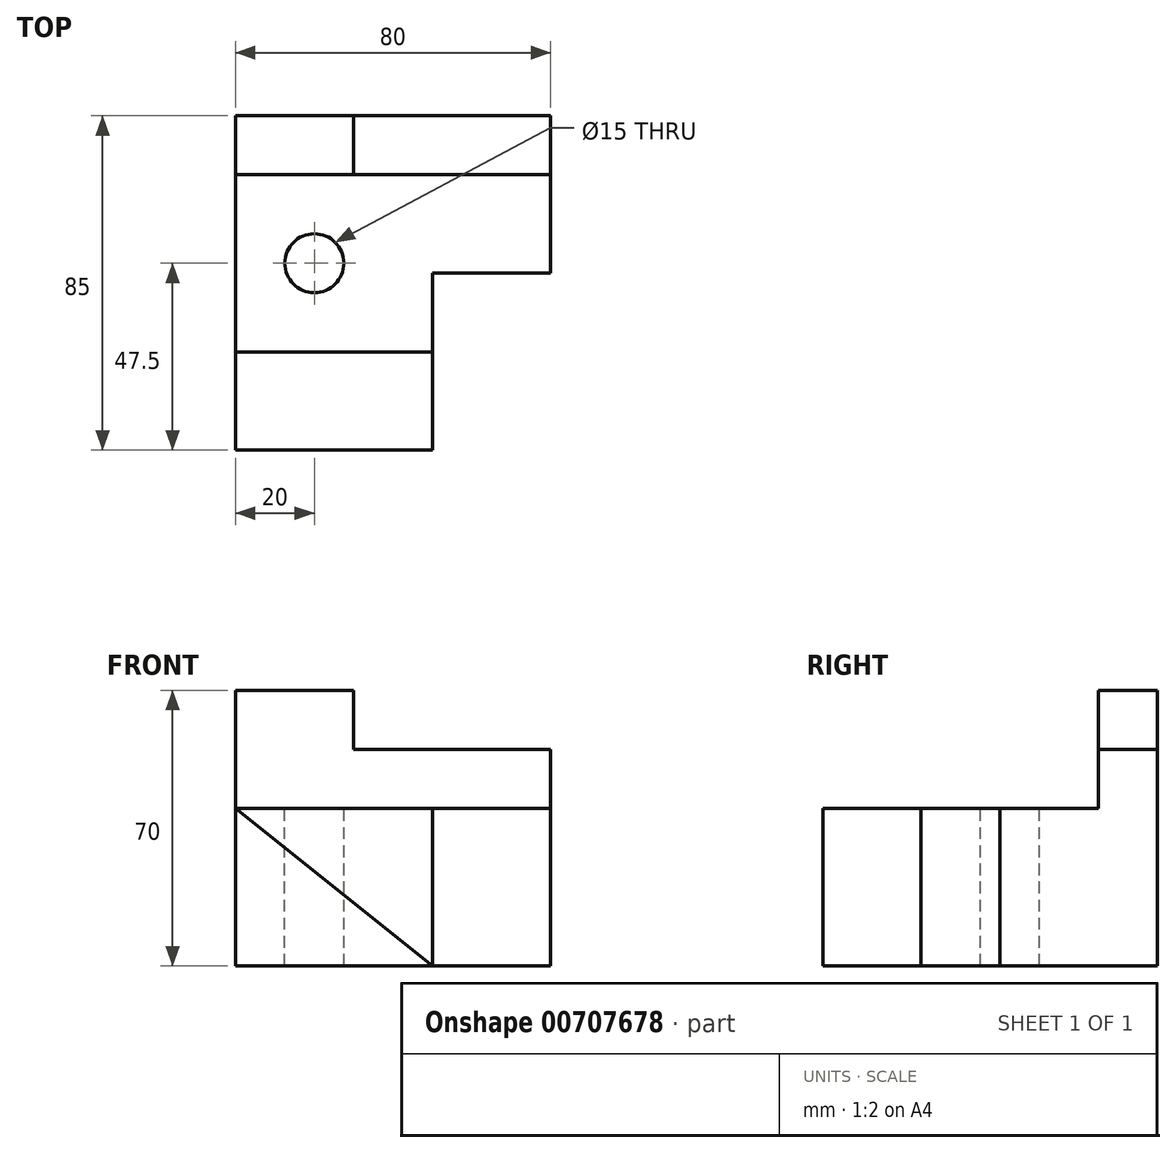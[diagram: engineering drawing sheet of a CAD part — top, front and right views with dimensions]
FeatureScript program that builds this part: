
annotation { "Feature Type Name" : "Feature", "Feature Type Description" : "" }
export const myFeature = defineFeature(function(context is Context, id is Id, definition is map)
    precondition{}
    {
        {
            var Q0;
            Q0=qCreatedBy(makeId("Front.planeOp"),FACE);
            var sketch = newSketch(context, id + "F0", { "sketchPlane" : qUnion([Q0])});
            skLineSegment(sketch, "E0", {"start": v(0, 0) * mm, "end": v(0, 40) * mm});
            skLineSegment(sketch, "E1", {"start": v(0, 0) * mm, "end": v(50, 0) * mm});
            skLineSegment(sketch, "E2", {"start": v(50, 0) * mm, "end": v(0, 40) * mm});
            skSolve(sketch);
        }
        {
            var Q0;
            Q0 = qSketchRegion(id + "F0", true);
            extrude(context, id + "F1", {"entities" : qUnion([Q0]), "oppositeDirection" : true, "depth" : 25 * mm, "offsetDistance" : 25 * mm});
        }
        {
            var Q0;
            Q0=qCreatedBy(makeId("Top.planeOp"),FACE);
            var sketch = newSketch(context, id + "F2", { "sketchPlane" : qUnion([Q0])});
            skLineSegment(sketch, "E3", {"start": v(0, 0) * mm, "end": v(0, 25) * mm});
            skLineSegment(sketch, "E4", {"start": v(0, 25) * mm, "end": v(0, 70) * mm});
            skLineSegment(sketch, "E5", {"start": v(0, 70) * mm, "end": v(80, 70) * mm});
            skLineSegment(sketch, "E6", {"start": v(80, 70) * mm, "end": v(80, 45) * mm});
            skLineSegment(sketch, "E7", {"start": v(50, 45) * mm, "end": v(80, 45) * mm});
            skLineSegment(sketch, "E8", {"start": v(50, 45) * mm, "end": v(50, 25) * mm});
            skLineSegment(sketch, "E9", {"start": v(50, 25) * mm, "end": v(0, 25) * mm});
            skSolve(sketch);
        }
        {
            var Q0;
            Q0 = qSketchRegion(id + "F2", true);
            extrude(context, id + "F3", {"entities" : qUnion([Q0]), "operationType" : NewBodyOperationType.ADD, "depth" : 40 * mm, "offsetDistance" : 25 * mm});
        }
        {
            var Q0;
            Q0=makeQuery(id+"F3.opExtrude","SWEPT_FACE",FACE,{"disambiguationData":[OSD([sQuery(id+"F2.wireOp",EDGE,"E5")])]});
            var sketch = newSketch(context, id + "F4", { "sketchPlane" : qUnion([Q0])});
            skLineSegment(sketch, "E10", {"start": v(0, 0) * mm, "end": v(0, 70) * mm});
            skLineSegment(sketch, "E11", {"start": v(0, 70) * mm, "end": v(-30, 70) * mm});
            skLineSegment(sketch, "E12", {"start": v(-30, 70) * mm, "end": v(-30, 55) * mm});
            skLineSegment(sketch, "E13", {"start": v(-30, 55) * mm, "end": v(-80, 55) * mm});
            skLineSegment(sketch, "E14", {"start": v(-80, 55) * mm, "end": v(-80, 40) * mm});
            skLineSegment(sketch, "E15", {"start": v(-80, 40) * mm, "end": v(-80, 0) * mm});
            skLineSegment(sketch, "E16", {"start": v(-80, 0) * mm, "end": v(0, 0) * mm});
            skSolve(sketch);
        }
        {
            var Q0;
            Q0 = qSketchRegion(id + "F4", true);
            extrude(context, id + "F5", {"entities" : qUnion([Q0]), "operationType" : NewBodyOperationType.ADD, "depth" : 15 * mm, "offsetDistance" : 25 * mm});
        }
        {
            var Q0;
            Q0=makeQuery(id+"F3.opExtrude","CAP_FACE",FACE,{"disambiguationData":[OSD([sQuery(id+"F2.wireOp",EDGE,"E4"),sQuery(id+"F2.wireOp",EDGE,"E5"),sQuery(id+"F2.wireOp",EDGE,"E6"),sQuery(id+"F2.wireOp",EDGE,"E7"),sQuery(id+"F2.wireOp",EDGE,"E8"),sQuery(id+"F2.wireOp",EDGE,"E9")])],"isStart":false});
            var sketch = newSketch(context, id + "F6", { "sketchPlane" : qUnion([Q0])});
            skLineSegment(sketch, "E17", {"start": v(0, 0) * mm, "end": v(0, 47.5) * mm});
            skCircle(sketch, "E18", {"center": v(20, 47.5) * mm, "radius": 7.5 * mm});
            skSolve(sketch);
        }
        {
            var Q0;
            Q0 = qSketchRegion(id + "F6", true);
            extrude(context, id + "F7", {"entities" : qUnion([Q0]), "operationType" : NewBodyOperationType.REMOVE, "oppositeDirection" : true, "depth" : 40 * mm, "offsetDistance" : 25 * mm});
        }
    });
